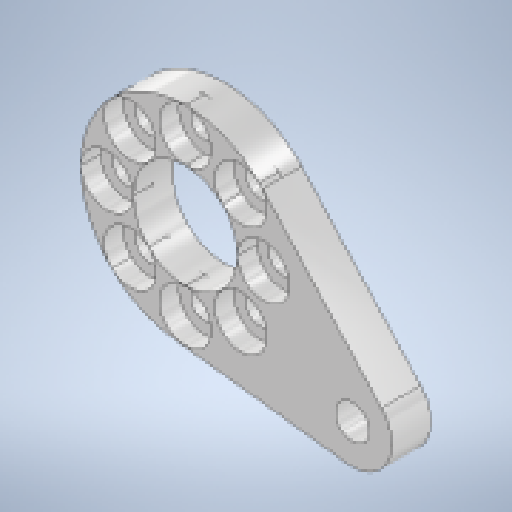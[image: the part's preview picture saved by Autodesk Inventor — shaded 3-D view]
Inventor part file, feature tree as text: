
AUTODESK INVENTOR PART (.ipt)
format: ipt  version: 2025.1 (Build 291241000, 241)  size: 237,056 bytes
history: native  units: mm
features: other x8, extrude x3, sketch x3, reference x2
ambient origin geometry x8: Origin, YZ Plane, XZ Plane, XY Plane, X Axis, Y Axis, Z Axis, Center Point
bodies: Body1 (feature_tree)
feature tree (16):
  other  "ソリッド1"
  extrude  "押し出し1"  Depth=8.0mm
  extrude  "押し出し2"  Depth=16.0mm
  extrude  "押し出し3"  Depth=12.0mm
  sketch  "スケッチ1"
  other  "スケッチ円形状パターン1"
  sketch  "スケッチ2"
  sketch  "スケッチ3"
  reference  "参照2"
  reference  "参照3"
  other  "スケッチ円形状パターン2"
  other  "Assembly1"
  other  "kosipiti:2"
  other  "<userpath>\Documents\Inventor\Vixen\doutai.iam"
  other  "doutai.iam"
  other  "kosi_pti:1"
